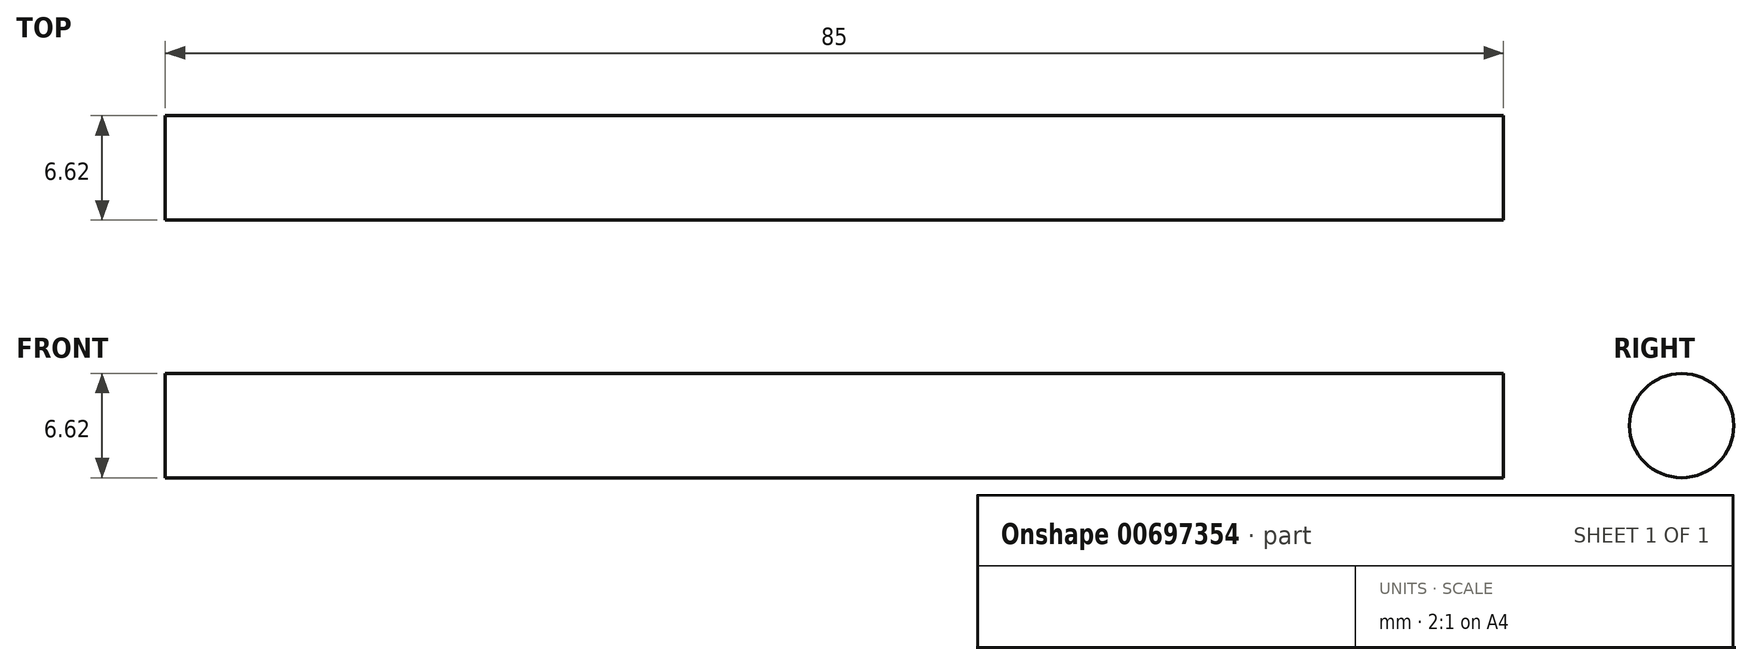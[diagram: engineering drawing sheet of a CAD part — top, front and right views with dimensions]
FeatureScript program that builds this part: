
annotation { "Feature Type Name" : "Feature", "Feature Type Description" : "" }
export const myFeature = defineFeature(function(context is Context, id is Id, definition is map)
    precondition{}
    {
        {
            var Q0;
            Q0=qCreatedBy(makeId("Right.planeOp"),FACE);
            var sketch = newSketch(context, id + "F0", { "sketchPlane" : qUnion([Q0])});
            skCircle(sketch, "E0", {"center": v(0, 0) * mm, "radius": 3.31 * mm});
            skSolve(sketch);
        }
        {
            var Q0;
            Q0 = qSketchRegion(id + "F0", true);
            extrude(context, id + "F1", {"entities" : qUnion([Q0]), "depth" : 85 * mm, "offsetDistance" : 25 * mm});
        }
    });
